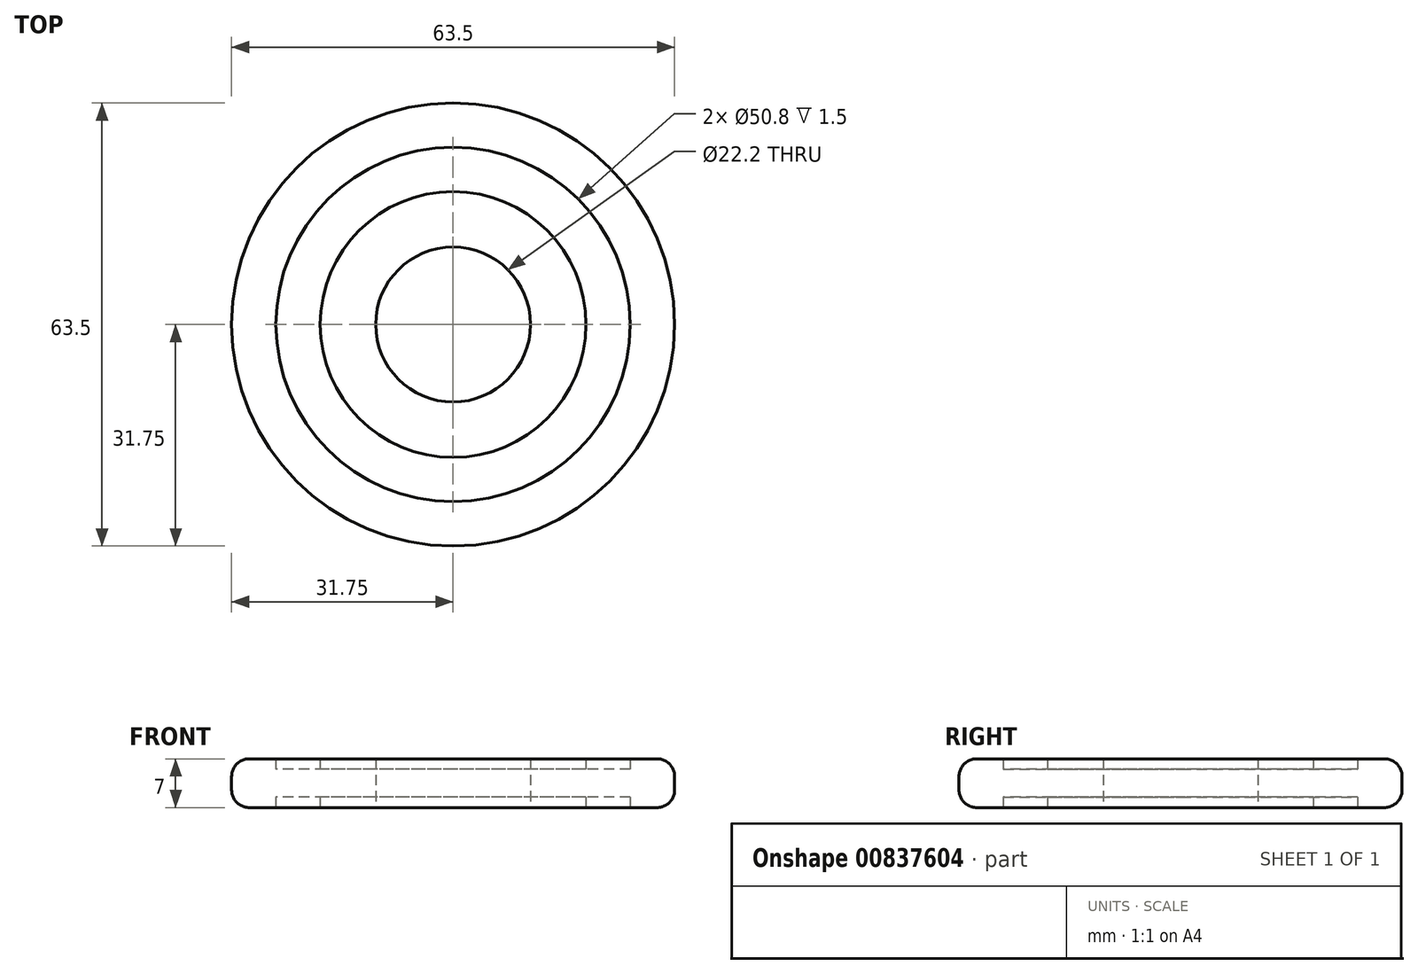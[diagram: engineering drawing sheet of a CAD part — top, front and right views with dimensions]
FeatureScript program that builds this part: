
annotation { "Feature Type Name" : "Feature", "Feature Type Description" : "" }
export const myFeature = defineFeature(function(context is Context, id is Id, definition is map)
    precondition{}
    {
        {
            var Q0;
            Q0=qCreatedBy(makeId("Top.planeOp"),FACE);
            var sketch = newSketch(context, id + "F0", { "sketchPlane" : qUnion([Q0])});
            skCircle(sketch, "E0", {"center": v(0, 0) * mm, "radius": 11.1 * mm});
            skCircle(sketch, "E1", {"center": v(0, 0) * mm, "radius": 31.75 * mm});
            skCircle(sketch, "E2", {"center": v(0, 0) * mm, "radius": 25.4 * mm});
            skCircle(sketch, "E3", {"center": v(0, 0) * mm, "radius": 19.05 * mm});
            skSolve(sketch);
        }
        {
            var Q0;
            Q0=makeQuery(id+"F0.imprint","IMPRINT",FACE,{"disambiguationData":[TD([[makeQuery(id+"F0.imprint","IMPRINT",EDGE,{"derivedFrom":sQuery(id+"F0.wireOp",EDGE,"E0")}),-1.0]])]});
            var Q1;
            Q1=makeQuery(id+"F0.imprint","IMPRINT",FACE,{"disambiguationData":[TD([[makeQuery(id+"F0.imprint","IMPRINT",EDGE,{"derivedFrom":sQuery(id+"F0.wireOp",EDGE,"E1")}),1.0]])]});
            extrude(context, id + "F1", {"entities" : qUnion([Q0, Q1]), "endBound" : BoundingType.SYMMETRIC, "depth" : 7 * mm, "offsetDistance" : 25.4 * mm});
        }
        {
            var Q0;
            Q0=makeQuery(id+"F0.imprint","IMPRINT",FACE,{"disambiguationData":[TD([[makeQuery(id+"F0.imprint","IMPRINT",EDGE,{"derivedFrom":sQuery(id+"F0.wireOp",EDGE,"E2")}),1.0]])]});
            extrude(context, id + "F2", {"entities" : qUnion([Q0]), "endBound" : BoundingType.SYMMETRIC, "depth" : 4 * mm, "offsetDistance" : 25.4 * mm});
        }
        {
            var Q0;
            Q0=makeQuery(id+"F0.imprint","IMPRINT",FACE,{"disambiguationData":[TD([[makeQuery(id+"F0.imprint","IMPRINT",EDGE,{"derivedFrom":sQuery(id+"F0.wireOp",EDGE,"E2")}),1.0]])]});
            extrude(context, id + "F3", {"entities" : qUnion([Q0]), "operationType" : NewBodyOperationType.ADD, "oppositeDirection" : true, "depth" : .2 * mm, "offsetDistance" : 25.4 * mm});
        }
        {
            var Q0;
            Q0=makeQuery(id+"F1.opExtrude","CAP_EDGE",EDGE,{"disambiguationData":[OSD([sQuery(id+"F0.wireOp",EDGE,"E1")])],"isStart":false});
            var Q1;
            Q1=makeQuery(id+"F1.opExtrude","CAP_EDGE",EDGE,{"disambiguationData":[OSD([sQuery(id+"F0.wireOp",EDGE,"E1")])],"isStart":true});
            fillet(context, id + "F4", {"entities" : qUnion([Q0, Q1]), "radius" : 2.54 * mm, "tangentPropagation" : true, "allowEdgeOverflow" : false});
        }
    });
